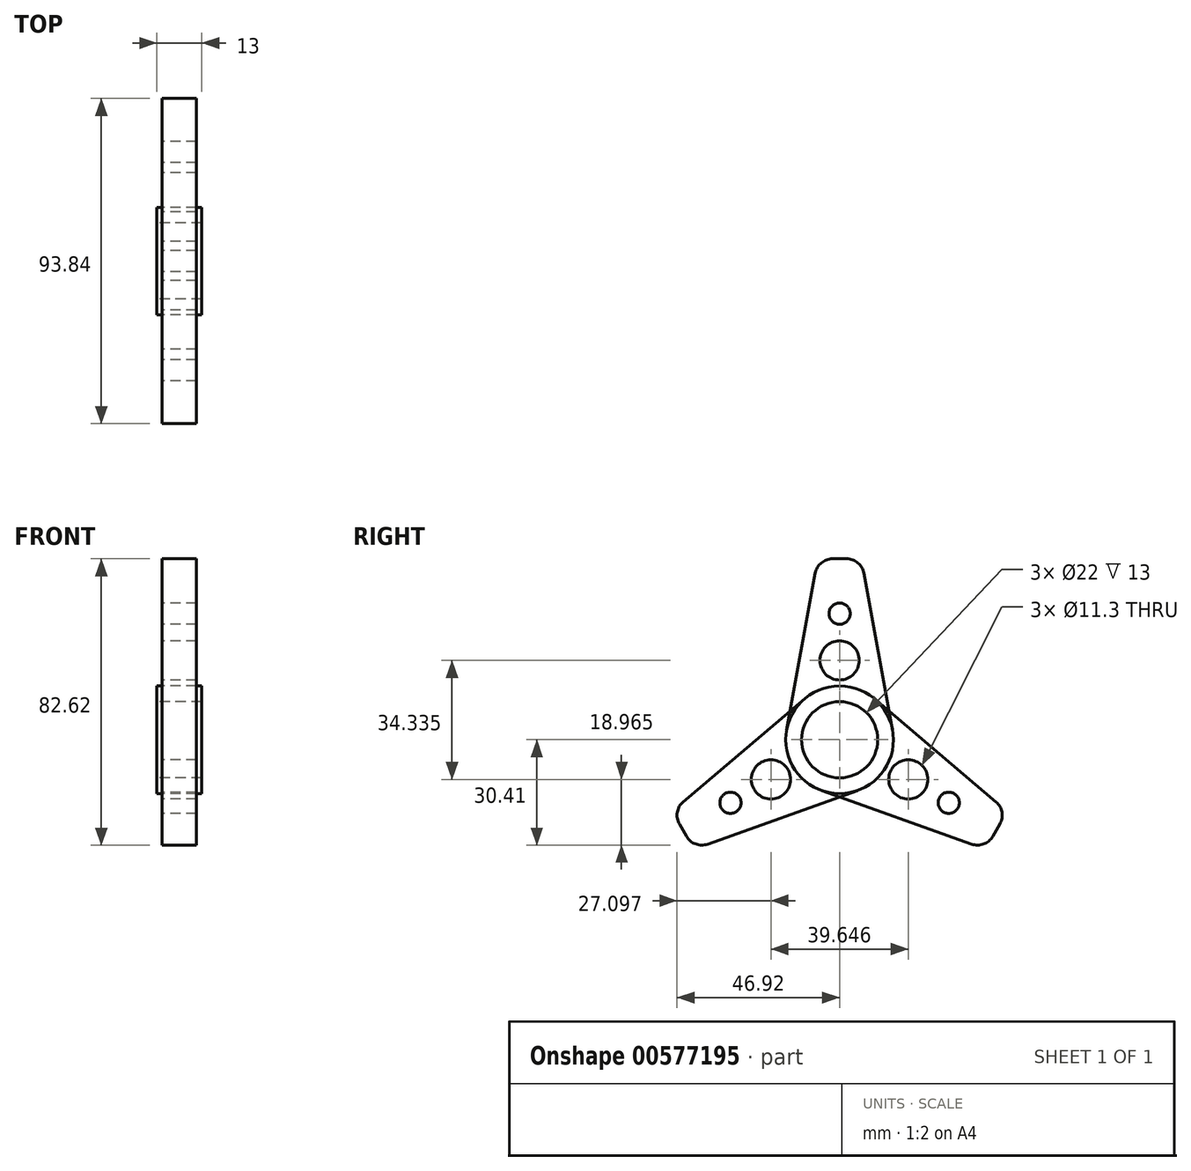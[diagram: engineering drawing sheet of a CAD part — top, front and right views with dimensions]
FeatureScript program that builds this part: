
annotation { "Feature Type Name" : "Feature", "Feature Type Description" : "" }
export const myFeature = defineFeature(function(context is Context, id is Id, definition is map)
    precondition{}
    {
        {
            var Q0;
            Q0=qCreatedBy(makeId("Right.planeOp"),FACE);
            var sketch = newSketch(context, id + "F0", { "sketchPlane" : qUnion([Q0])});
            skCircle(sketch, "E0", {"center": v(0, 0) * mm, "radius": 11 * mm});
            skCircle(sketch, "E1", {"center": v(0, 0) * mm, "radius": 15.53 * mm});
            skLineSegment(sketch, "E2", {"start": v(6.28, 52.21) * mm, "end": v(15.28, 2.78) * mm});
            skLineSegment(sketch, "E3", {"start": v(-6.28, 52.21) * mm, "end": v(-15.28, 2.78) * mm});
            skLineSegment(sketch, "E4", {"start": v(-6.28, 52.21) * mm, "end": v(6.28, 52.21) * mm});
            skCircle(sketch, "E5", {"center": v(0, 22.89) * mm, "radius": 5.65 * mm});
            skCircle(sketch, "E6", {"center": v(0, 36.38) * mm, "radius": 3.07 * mm});
            skSolve(sketch);
        }
        {
            var Q0;
            Q0=makeQuery(id+"F0.imprint","IMPRINT",FACE,{"disambiguationData":[TD([[makeQuery(id+"F0.imprint","IMPRINT",EDGE,{"derivedFrom":sQuery(id+"F0.wireOp",EDGE,"E0")}),-1.0]])]});
            extrude(context, id + "F1", {"entities" : qUnion([Q0]), "depth" : 6.5 * mm, "offsetDistance" : 25.4 * mm, "hasSecondDirection" : true, "secondDirectionOppositeDirection" : true, "secondDirectionDepth" : 6.5 * mm});
        }
        {
            var Q0;
            {var subQ0=sQuery(id+"F0.wireOp",EDGE,"E2");Q0=makeQuery(id+"F0.imprint","IMPRINT",FACE,{"disambiguationData":[TD([[makeQuery(id+"F0.imprint","IMPRINT",EDGE,{"derivedFrom":subQ0}),-1.0]])]});}
            extrude(context, id + "F2", {"entities" : qUnion([Q0]), "operationType" : NewBodyOperationType.ADD, "depth" : 5 * mm, "offsetDistance" : 25.4 * mm, "hasSecondDirection" : true, "secondDirectionOppositeDirection" : true, "secondDirectionDepth" : 5 * mm});
        }
        {
            var Q0;
            Q0=makeQuery(id+"F2.opExtrude","SWEPT_EDGE",EDGE,{"disambiguationData":[OSD([sQuery(id+"F0.wireOp",EDGE,"E2"),sQuery(id+"F0.wireOp",EDGE,"E4")])]});
            var Q1;
            Q1=makeQuery(id+"F2.opExtrude","SWEPT_EDGE",EDGE,{"disambiguationData":[OSD([sQuery(id+"F0.wireOp",EDGE,"E3"),sQuery(id+"F0.wireOp",EDGE,"E4")])]});
            fillet(context, id + "F3", {"entities" : qUnion([Q0, Q1]), "radius" : 5.08 * mm, "tangentPropagation" : true, "allowEdgeOverflow" : false});
        }
        {
            var Q0;
            Q0=makeQuery(id+"F1.opExtrude","SWEPT_BODY",BODY,{"disambiguationData":[OSD([sQuery(id+"F0.wireOp",EDGE,"E0"),sQuery(id+"F0.wireOp",EDGE,"E1")])]});
            var Q1;
            Q1=makeQuery(id+"F1.opExtrude","CAP_EDGE",EDGE,{"disambiguationData":[OSD([sQuery(id+"F0.wireOp",EDGE,"E1")])],"isStart":false});
            circularPattern(context, id + "F4", {"entities" : qUnion([Q0]), "axis" : qUnion([Q1]), "angle" : 360 * degree, "instanceCount" : 3, "equalSpace" : true});
        }
    });
